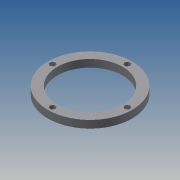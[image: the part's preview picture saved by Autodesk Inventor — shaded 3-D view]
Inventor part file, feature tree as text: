
AUTODESK INVENTOR PART (.ipt)
format: ipt  version: 2013 (Build 170138000, 138)  size: 121,856 bytes
history: native  units: mm
features: extrude x3, sketch x3, pattern_circular x1
ambient origin geometry x8: Origin, YZ Plane, XZ Plane, XY Plane, X Axis, Y Axis, Z Axis, Center Point
bodies: Solid1 (feature_tree)
feature tree (7):
  extrude  "Extrusion1"  Depth=90.0mm
  extrude  "Extrusion2"  Depth=40.0mm
  extrude  "Extrusion3"  Depth=10.0mm TaperAngle=0.0deg
  pattern_circular  "Circular Pattern1"  [2 undecoded]
  sketch  "Sketch1"  dims[d0=70.0mm d2=90.0mm]
  sketch  "Sketch2"  dims[d3=8.0mm d4=0.0mm d5=40.0mm]
  sketch  "Sketch3"  dims[d6=3.5mm d7=10.0mm d8=0.0mm d9=5.5mm d10=4.0mm d11=0.0mm d12=40.0mm d13=360.0deg]
note: 2 required parameter values undecoded (feature->parameter linkage not recoverable at this tier; creation-order binding heuristic only, values carry confidence <= 0.55)
